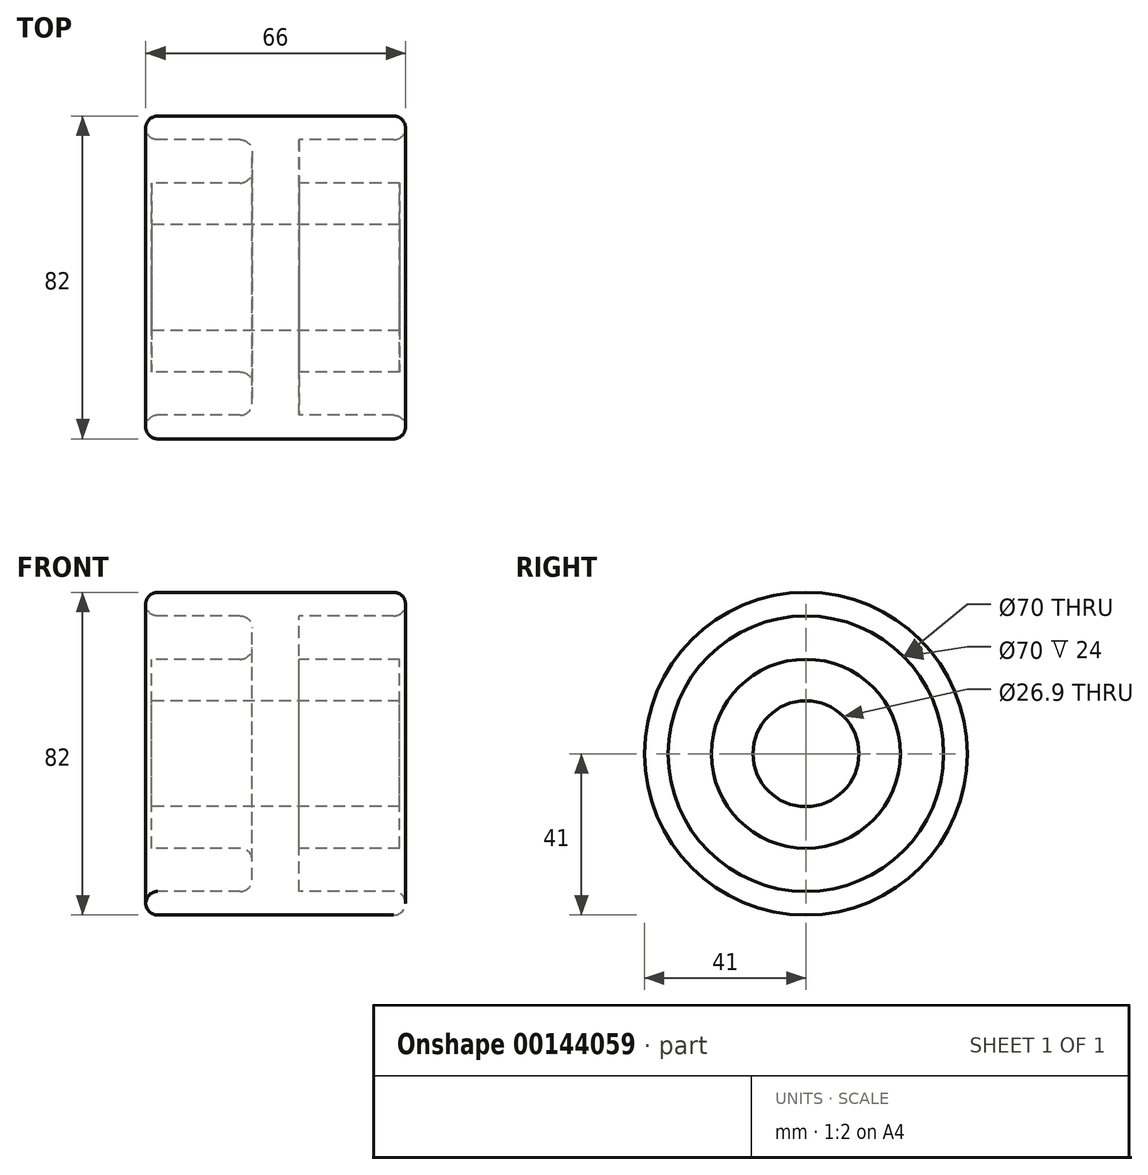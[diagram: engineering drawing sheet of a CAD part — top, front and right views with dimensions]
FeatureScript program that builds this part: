
annotation { "Feature Type Name" : "Feature", "Feature Type Description" : "" }
export const myFeature = defineFeature(function(context is Context, id is Id, definition is map)
    precondition{}
    {
        {
            var Q0;
            Q0=qCreatedBy(makeId("Right.planeOp"),FACE);
            var sketch = newSketch(context, id + "F0", { "sketchPlane" : qUnion([Q0])});
            skCircle(sketch, "E0", {"center": v(0, 0) * mm, "radius": 13.45 * mm});
            skCircle(sketch, "E1", {"center": v(0, 0) * mm, "radius": 24 * mm});
            skCircle(sketch, "E2", {"center": v(0, 0) * mm, "radius": 35 * mm});
            skCircle(sketch, "E3", {"center": v(0, 0) * mm, "radius": 41 * mm});
            skSolve(sketch);
        }
        {
            var Q0;
            Q0=makeQuery(id+"F0.imprint","IMPRINT",FACE,{"disambiguationData":[TD([[makeQuery(id+"F0.imprint","IMPRINT",EDGE,{"derivedFrom":sQuery(id+"F0.wireOp",EDGE,"E2")}),-1.0]])]});
            extrude(context, id + "F1", {"entities" : qUnion([Q0]), "endBound" : BoundingType.SYMMETRIC, "depth" : 66 * mm});
        }
        {
            var Q0;
            Q0=makeQuery(id+"F0.imprint","IMPRINT",FACE,{"disambiguationData":[TD([[makeQuery(id+"F0.imprint","IMPRINT",EDGE,{"derivedFrom":sQuery(id+"F0.wireOp",EDGE,"E0")}),-1.0]])]});
            extrude(context, id + "F2", {"entities" : qUnion([Q0]), "operationType" : NewBodyOperationType.ADD, "endBound" : BoundingType.SYMMETRIC, "depth" : 63 * mm});
        }
        {
            var Q0;
            Q0=makeQuery(id+"F0.imprint","IMPRINT",FACE,{"disambiguationData":[TD([[makeQuery(id+"F0.imprint","IMPRINT",EDGE,{"derivedFrom":sQuery(id+"F0.wireOp",EDGE,"E1")}),-1.0]])]});
            extrude(context, id + "F3", {"entities" : qUnion([Q0]), "operationType" : NewBodyOperationType.ADD, "endBound" : BoundingType.SYMMETRIC, "depth" : 12 * mm});
        }
        {
            var Q0;
            Q0=makeQuery(id+"F1.opExtrude","CAP_EDGE",EDGE,{"disambiguationData":[OSD([sQuery(id+"F0.wireOp",EDGE,"E2")])],"isStart":false});
            var Q1;
            Q1=makeQuery(id+"F3.opExtrude","CAP_EDGE",EDGE,{"disambiguationData":[OSD([sQuery(id+"F0.wireOp",EDGE,"E1")])],"isStart":false});
            var Q2;
            Q2=makeQuery(id+"F3.opExtrude","CAP_EDGE",EDGE,{"disambiguationData":[OSD([sQuery(id+"F0.wireOp",EDGE,"E2")])],"isStart":false});
            var Q3;
            Q3=makeQuery(id+"F1.opExtrude","CAP_EDGE",EDGE,{"disambiguationData":[OSD([sQuery(id+"F0.wireOp",EDGE,"E3")])],"isStart":false});
            var Q4;
            Q4=makeQuery(id+"F3.opExtrude","CAP_EDGE",EDGE,{"disambiguationData":[OSD([sQuery(id+"F0.wireOp",EDGE,"E2")])],"isStart":true});
            var Q5;
            Q5=makeQuery(id+"F3.opExtrude","CAP_EDGE",EDGE,{"disambiguationData":[OSD([sQuery(id+"F0.wireOp",EDGE,"E1")])],"isStart":true});
            var Q6;
            Q6=makeQuery(id+"F1.opExtrude","CAP_EDGE",EDGE,{"disambiguationData":[OSD([sQuery(id+"F0.wireOp",EDGE,"E2")])],"isStart":true});
            var Q7;
            Q7=makeQuery(id+"F1.opExtrude","CAP_EDGE",EDGE,{"disambiguationData":[OSD([sQuery(id+"F0.wireOp",EDGE,"E3")])],"isStart":true});
            fillet(context, id + "F4", {"entities" : qUnion([Q0, Q1, Q2, Q3, Q4, Q5, Q6, Q7]), "radius" : 3 * mm, "tangentPropagation" : true, "allowEdgeOverflow" : false});
        }
    });
